# Revit family: Caribou_Mercury_Semi Recessed 2_0
name_source: partatom
category: Lighting Fixtures
units: mm (PartAtom-declared; Revit-internal decimal feet)

## family parameters
Always vertical = Yes
Cut with Voids When Loaded = No
Host = Ceiling
Light Source = Yes
Maintain Annotation Orientation = No
OmniClass Number = 23.80.70.11
OmniClass Title = Luminaries for Internal Lighting
Part Type = Normal
Room Calculation Point = No
Round Connector Dimension = Use Diameter
Shared = No

## types (2) — shared parameters
Angle (Use Tilt Angle) = 59.70°
Color Filter = 16777215
Dimming Lamp Color Temperature Shift = <None>
Light = Light
Light Source Symbol Length = 3048 mm  [stored 10 ft]
Manufacturer = Caribou
Spot Beam Angle = 30.00°
Spot Field Angle = 80.00°
Tilt Angle = 60.00°
zero-valued in all types: Default Elevation

## per-type parameters (varying)
| type | Light_Finishes | Model |
| Caribou Flat White | Caribou_Flat White | Mercury 2.0 Flat White |
| Caribou Ace Black | Caribou_Ace Black | Mercury 2.0 Ace Black |

note: [stored X ft] marks values corroborated as IEEE doubles in the binary element streams (Revit-internal decimal feet)

## geometry (parser evidence)
native form markers: Sweep x2
no freeform markers — native parametric forms only
